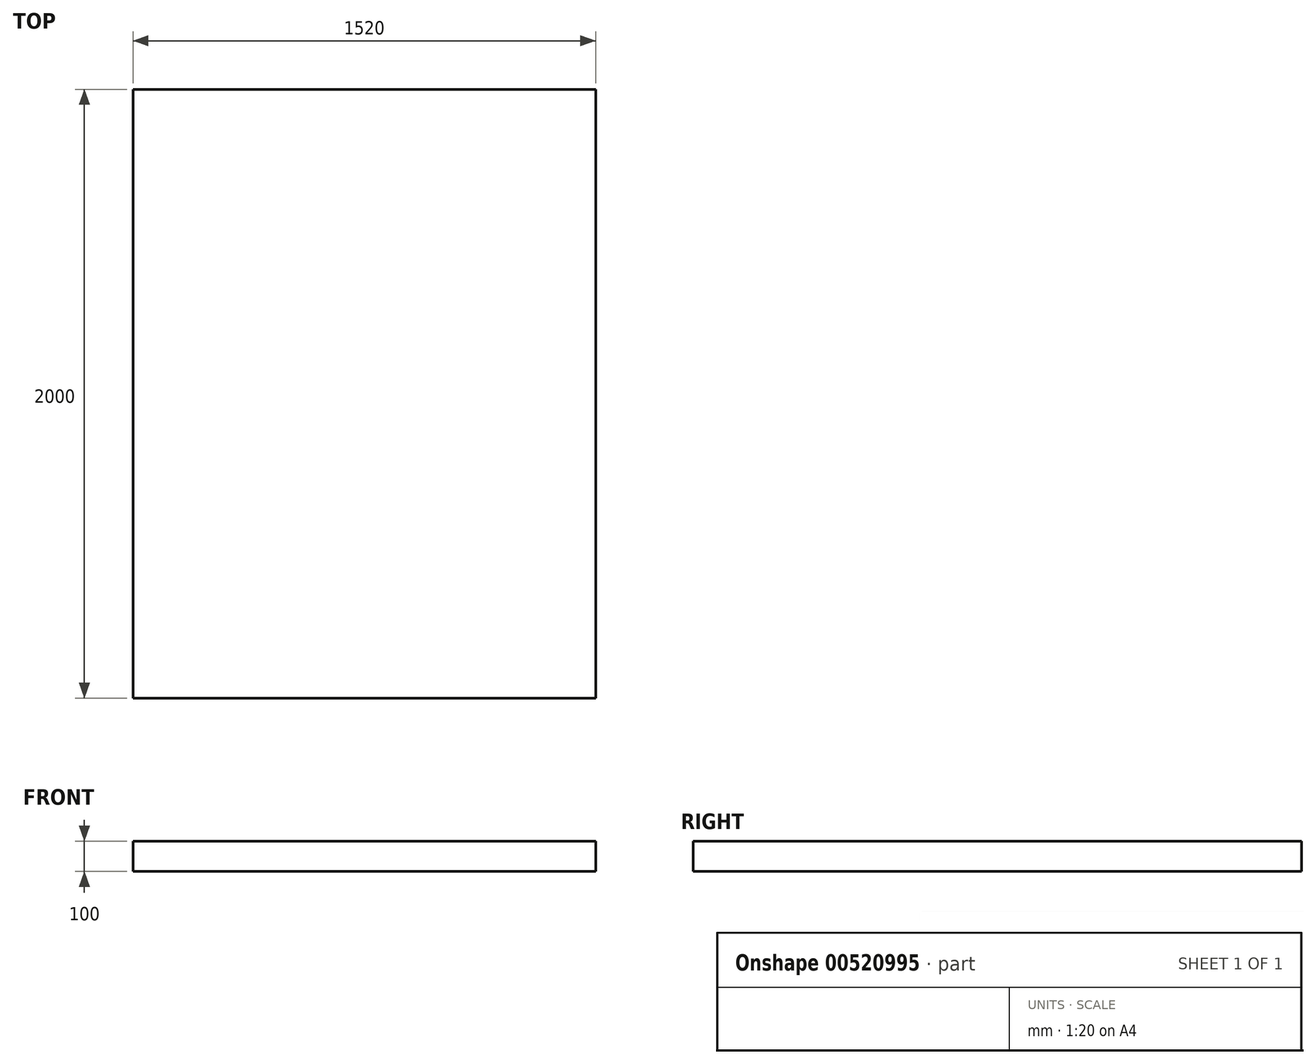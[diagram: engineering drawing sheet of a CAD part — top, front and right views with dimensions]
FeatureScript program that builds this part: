
annotation { "Feature Type Name" : "Feature", "Feature Type Description" : "" }
export const myFeature = defineFeature(function(context is Context, id is Id, definition is map)
    precondition{}
    {
        {
            var Q0;
            Q0=qCreatedBy(makeId("Top.planeOp"),FACE);
            var sketch = newSketch(context, id + "F0", { "sketchPlane" : qUnion([Q0])});
            skLineSegment(sketch, "E0.bottom", {"start": v(-760, 1000) * mm, "end": v(760, 1000) * mm});
            skLineSegment(sketch, "E0.top", {"start": v(-760, -1000) * mm, "end": v(760, -1000) * mm});
            skLineSegment(sketch, "E0.left", {"start": v(-760, 1000) * mm, "end": v(-760, -1000) * mm});
            skLineSegment(sketch, "E0.right", {"start": v(760, 1000) * mm, "end": v(760, -1000) * mm});
            skPoint(sketch, "E0.middle", {"position": v(0, 0) * mm});
            skSolve(sketch);
        }
        {
            var Q0;
            Q0 = qSketchRegion(id + "F0", true);
            extrude(context, id + "F1", {"entities" : qUnion([Q0]), "depth" : 100 * mm, "offsetDistance" : 25 * mm});
        }
    });
